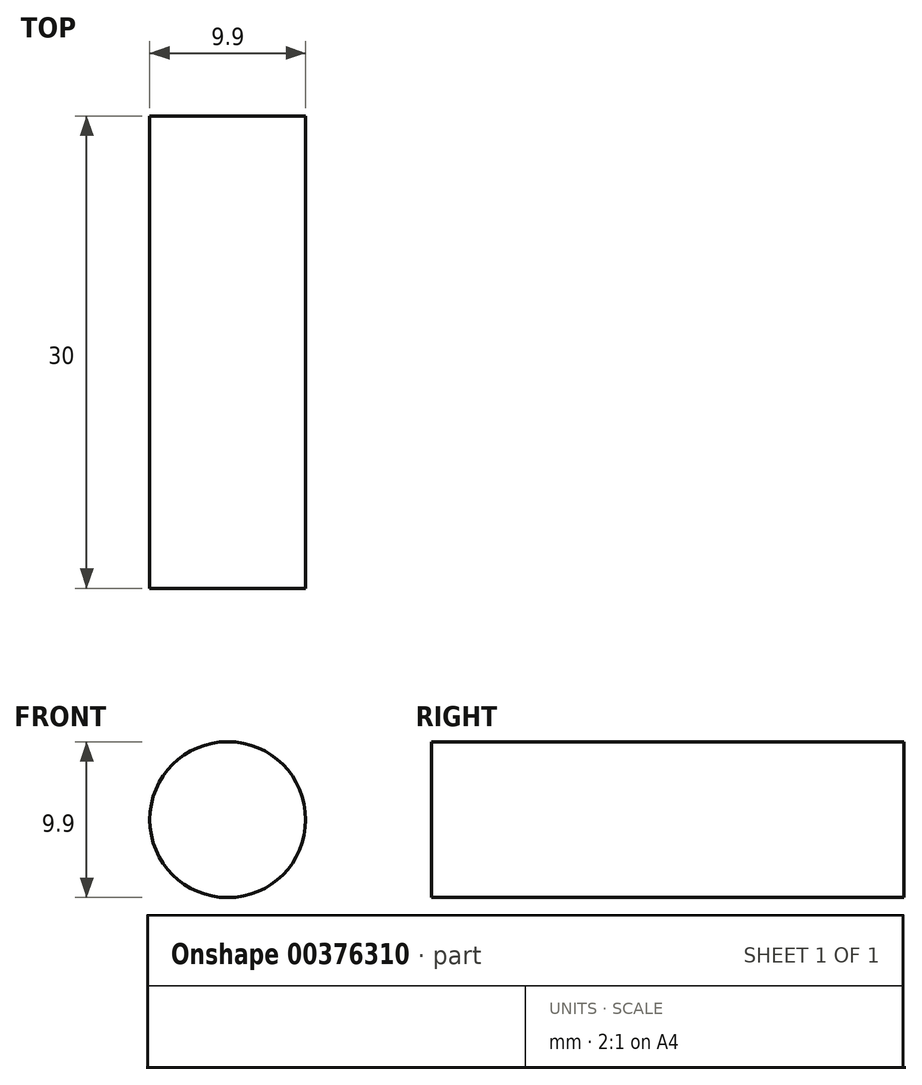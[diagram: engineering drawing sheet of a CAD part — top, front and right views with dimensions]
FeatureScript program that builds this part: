
annotation { "Feature Type Name" : "Feature", "Feature Type Description" : "" }
export const myFeature = defineFeature(function(context is Context, id is Id, definition is map)
    precondition{}
    {
        {
            var Q0;
            Q0=qCreatedBy(makeId("Front.planeOp"),FACE);
            var sketch = newSketch(context, id + "F0", { "sketchPlane" : qUnion([Q0])});
            skCircle(sketch, "E0", {"center": v(0, 0) * mm, "radius": 4.95 * mm});
            skSolve(sketch);
        }
        {
            var Q0;
            Q0 = qSketchRegion(id + "F0", true);
            extrude(context, id + "F1", {"entities" : qUnion([Q0]), "endBound" : BoundingType.SYMMETRIC, "depth" : 30 * mm});
        }
    });
